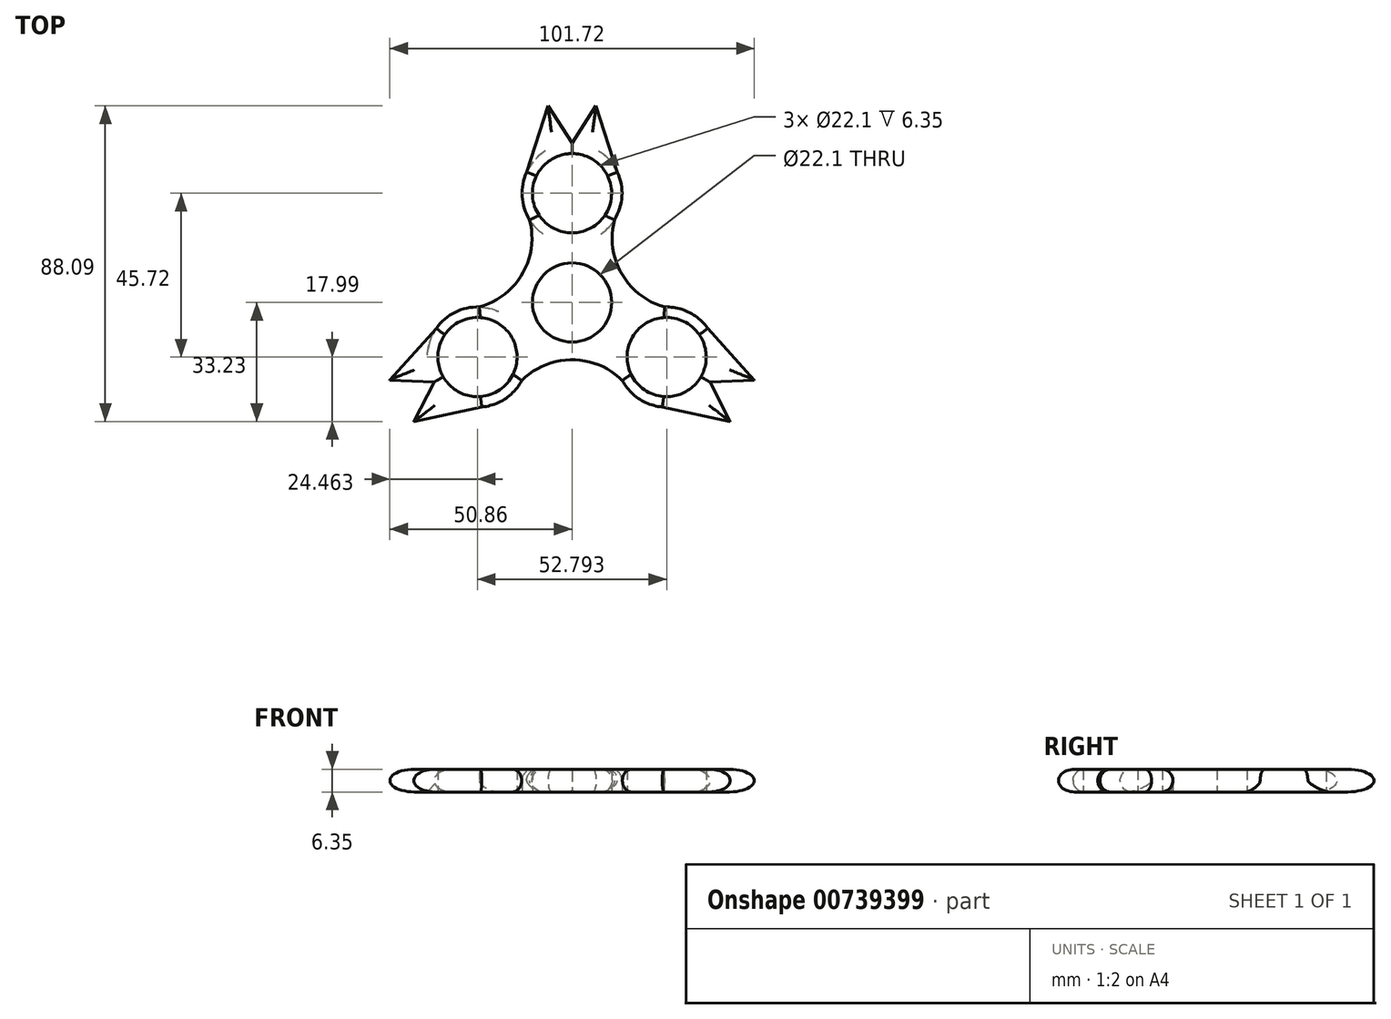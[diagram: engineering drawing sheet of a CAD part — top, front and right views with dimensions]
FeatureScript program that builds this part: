
annotation { "Feature Type Name" : "Feature", "Feature Type Description" : "" }
export const myFeature = defineFeature(function(context is Context, id is Id, definition is map)
    precondition{}
    {
        {
            var Q0;
            Q0=qCreatedBy(makeId("Top.planeOp"),FACE);
            var sketch = newSketch(context, id + "F0", { "sketchPlane" : qUnion([Q0])});
            skCircle(sketch, "E0", {"center": v(0, 0) * mm, "radius": 11.05 * mm});
            skLineSegment(sketch, "E1", {"start": v(0, 0) * mm, "end": v(0, 30.48) * mm});
            skCircle(sketch, "E2", {"center": v(0, 30.48) * mm, "radius": 11.05 * mm});
            skArc(sketch, "E3", {"start": v(-12.66, 36.38) * mm, "mid": v(-13.94, 29.62) * mm, "end": v(-11.84, 23.06) * mm});
            skCircle(sketch, "E4.1.0", {"center": v(-26.4, -15.24) * mm, "radius": 11.05 * mm});
            skArc(sketch, "E4.1.1", {"start": v(-25.17, -29.16) * mm, "mid": v(-18.68, -26.88) * mm, "end": v(-14.05, -21.79) * mm});
            skCircle(sketch, "E4.2.0", {"center": v(26.4, -15.24) * mm, "radius": 11.05 * mm});
            skArc(sketch, "E4.2.1", {"start": v(14.05, -21.79) * mm, "mid": v(18.68, -26.88) * mm, "end": v(25.17, -29.16) * mm});
            skLineSegment(sketch, "E5", {"start": v(0, 0) * mm, "end": v(-44.44, 25.66) * mm});
            skArc(sketch, "E6", {"start": v(-30.75, -1.97) * mm, "mid": v(-13.84, 8) * mm, "end": v(-13.67, 27.61) * mm});
            skArc(sketch, "E7.1.0", {"start": v(17.08, -25.65) * mm, "mid": v(0, -15.98) * mm, "end": v(-17.08, -25.65) * mm});
            skArc(sketch, "E7.2.0", {"start": v(13.67, 27.61) * mm, "mid": v(13.84, 8) * mm, "end": v(30.75, -1.97) * mm});
            skLineSegment(sketch, "E8", {"start": v(-12.66, 36.38) * mm, "end": v(-6.7, 54.86) * mm});
            skLineSegment(sketch, "E9", {"start": v(-6.7, 54.86) * mm, "end": v(0, 44.45) * mm});
            skLineSegment(sketch, "E10.MirrorCS", {"start": v(12.66, 36.38) * mm, "end": v(6.7, 54.86) * mm});
            skLineSegment(sketch, "E11.MirrorCS", {"start": v(6.7, 54.86) * mm, "end": v(0, 44.45) * mm});
            skLineSegment(sketch, "E12.1.0", {"start": v(-25.17, -29.16) * mm, "end": v(-44.17, -33.23) * mm});
            skLineSegment(sketch, "E12.1.1", {"start": v(-44.17, -33.23) * mm, "end": v(-38.5, -22.22) * mm});
            skLineSegment(sketch, "E12.1.2", {"start": v(-50.86, -21.64) * mm, "end": v(-38.5, -22.22) * mm});
            skLineSegment(sketch, "E12.1.3", {"start": v(-37.84, -7.22) * mm, "end": v(-50.86, -21.64) * mm});
            skLineSegment(sketch, "E12.2.0", {"start": v(37.84, -7.22) * mm, "end": v(50.86, -21.64) * mm});
            skLineSegment(sketch, "E12.2.1", {"start": v(50.86, -21.64) * mm, "end": v(38.5, -22.23) * mm});
            skLineSegment(sketch, "E12.2.2", {"start": v(44.17, -33.23) * mm, "end": v(38.5, -22.23) * mm});
            skLineSegment(sketch, "E12.2.3", {"start": v(25.17, -29.16) * mm, "end": v(44.17, -33.23) * mm});
            skArc(sketch, "E13.trimOffspring", {"start": v(11.84, 23.06) * mm, "mid": v(13.94, 29.62) * mm, "end": v(12.66, 36.38) * mm});
            skArc(sketch, "E14.trimOffspring", {"start": v(-25.9, -1.28) * mm, "mid": v(-32.62, -2.73) * mm, "end": v(-37.84, -7.22) * mm});
            skArc(sketch, "E15.trimOffspring", {"start": v(37.84, -7.22) * mm, "mid": v(32.62, -2.73) * mm, "end": v(25.9, -1.28) * mm});
            skSolve(sketch);
        }
        {
            var Q0;
            Q0 = qSketchRegion(id + "F0", true);
            extrude(context, id + "F1", {"entities" : qUnion([Q0]), "depth" : 6.35 * mm, "offsetDistance" : 25.4 * mm});
        }
        {
            var Q0;
            Q0=makeQuery(id+"F1.opExtrude","CAP_EDGE",EDGE,{"disambiguationData":[OSD([sQuery(id+"F0.wireOp",EDGE,"E3")])],"isStart":false});
            var Q1;
            Q1=makeQuery(id+"F1.opExtrude","CAP_EDGE",EDGE,{"disambiguationData":[OSD([sQuery(id+"F0.wireOp",EDGE,"E6")])],"isStart":false});
            var Q2;
            Q2=makeQuery(id+"F1.opExtrude","CAP_EDGE",EDGE,{"disambiguationData":[OSD([sQuery(id+"F0.wireOp",EDGE,"E14.trimOffspring")])],"isStart":false});
            var Q3;
            Q3=makeQuery(id+"F1.opExtrude","CAP_EDGE",EDGE,{"disambiguationData":[OSD([sQuery(id+"F0.wireOp",EDGE,"E6")])],"isStart":true});
            var Q4;
            Q4=makeQuery(id+"F1.opExtrude","CAP_EDGE",EDGE,{"disambiguationData":[OSD([sQuery(id+"F0.wireOp",EDGE,"E7.2.0")])],"isStart":false});
            var Q5;
            Q5=makeQuery(id+"F1.opExtrude","CAP_EDGE",EDGE,{"disambiguationData":[OSD([sQuery(id+"F0.wireOp",EDGE,"E13.trimOffspring")])],"isStart":false});
            var Q6;
            Q6=makeQuery(id+"F1.opExtrude","CAP_EDGE",EDGE,{"disambiguationData":[OSD([sQuery(id+"F0.wireOp",EDGE,"E7.2.0")])],"isStart":true});
            var Q7;
            Q7=makeQuery(id+"F1.opExtrude","CAP_EDGE",EDGE,{"disambiguationData":[OSD([sQuery(id+"F0.wireOp",EDGE,"E15.trimOffspring")])],"isStart":true});
            var Q8;
            Q8=makeQuery(id+"F1.opExtrude","CAP_EDGE",EDGE,{"disambiguationData":[OSD([sQuery(id+"F0.wireOp",EDGE,"E4.2.1")])],"isStart":false});
            var Q9;
            Q9=makeQuery(id+"F1.opExtrude","CAP_EDGE",EDGE,{"disambiguationData":[OSD([sQuery(id+"F0.wireOp",EDGE,"E7.1.0")])],"isStart":false});
            var Q10;
            Q10=makeQuery(id+"F1.opExtrude","CAP_EDGE",EDGE,{"disambiguationData":[OSD([sQuery(id+"F0.wireOp",EDGE,"E4.1.1")])],"isStart":false});
            var Q11;
            Q11=makeQuery(id+"F1.opExtrude","CAP_EDGE",EDGE,{"disambiguationData":[OSD([sQuery(id+"F0.wireOp",EDGE,"E7.1.0")])],"isStart":true});
            var Q12;
            Q12=makeQuery(id+"F1.opExtrude","CAP_EDGE",EDGE,{"disambiguationData":[OSD([sQuery(id+"F0.wireOp",EDGE,"E4.1.1")])],"isStart":true});
            var Q13;
            Q13=makeQuery(id+"F1.opExtrude","CAP_EDGE",EDGE,{"disambiguationData":[OSD([sQuery(id+"F0.wireOp",EDGE,"E4.2.1")])],"isStart":true});
            var Q14;
            Q14=makeQuery(id+"F1.opExtrude","CAP_EDGE",EDGE,{"disambiguationData":[OSD([sQuery(id+"F0.wireOp",EDGE,"E12.1.3")])],"isStart":true});
            var Q15;
            Q15=makeQuery(id+"F1.opExtrude","CAP_EDGE",EDGE,{"disambiguationData":[OSD([sQuery(id+"F0.wireOp",EDGE,"E12.1.2")])],"isStart":true});
            var Q16;
            Q16=makeQuery(id+"F1.opExtrude","CAP_EDGE",EDGE,{"disambiguationData":[OSD([sQuery(id+"F0.wireOp",EDGE,"E12.1.0")])],"isStart":true});
            var Q17;
            Q17=makeQuery(id+"F1.opExtrude","CAP_EDGE",EDGE,{"disambiguationData":[OSD([sQuery(id+"F0.wireOp",EDGE,"E12.1.1")])],"isStart":true});
            var Q18;
            Q18=makeQuery(id+"F1.opExtrude","CAP_EDGE",EDGE,{"disambiguationData":[OSD([sQuery(id+"F0.wireOp",EDGE,"E12.2.3")])],"isStart":true});
            var Q19;
            Q19=makeQuery(id+"F1.opExtrude","CAP_EDGE",EDGE,{"disambiguationData":[OSD([sQuery(id+"F0.wireOp",EDGE,"E12.2.2")])],"isStart":true});
            var Q20;
            Q20=makeQuery(id+"F1.opExtrude","CAP_EDGE",EDGE,{"disambiguationData":[OSD([sQuery(id+"F0.wireOp",EDGE,"E12.2.1")])],"isStart":true});
            var Q21;
            Q21=makeQuery(id+"F1.opExtrude","CAP_EDGE",EDGE,{"disambiguationData":[OSD([sQuery(id+"F0.wireOp",EDGE,"E12.2.0")])],"isStart":true});
            var Q22;
            Q22=makeQuery(id+"F1.opExtrude","CAP_EDGE",EDGE,{"disambiguationData":[OSD([sQuery(id+"F0.wireOp",EDGE,"E10.MirrorCS")])],"isStart":true});
            var Q23;
            Q23=makeQuery(id+"F1.opExtrude","CAP_EDGE",EDGE,{"disambiguationData":[OSD([sQuery(id+"F0.wireOp",EDGE,"E8")])],"isStart":true});
            var Q24;
            Q24=makeQuery(id+"F1.opExtrude","CAP_EDGE",EDGE,{"disambiguationData":[OSD([sQuery(id+"F0.wireOp",EDGE,"E11.MirrorCS")])],"isStart":true});
            var Q25;
            Q25=makeQuery(id+"F1.opExtrude","CAP_EDGE",EDGE,{"disambiguationData":[OSD([sQuery(id+"F0.wireOp",EDGE,"E9")])],"isStart":true});
            var Q26;
            Q26=makeQuery(id+"F1.opExtrude","CAP_EDGE",EDGE,{"disambiguationData":[OSD([sQuery(id+"F0.wireOp",EDGE,"E12.2.3")])],"isStart":false});
            var Q27;
            Q27=makeQuery(id+"F1.opExtrude","CAP_EDGE",EDGE,{"disambiguationData":[OSD([sQuery(id+"F0.wireOp",EDGE,"E12.1.0")])],"isStart":false});
            var Q28;
            Q28=makeQuery(id+"F1.opExtrude","CAP_EDGE",EDGE,{"disambiguationData":[OSD([sQuery(id+"F0.wireOp",EDGE,"E12.1.3")])],"isStart":false});
            var Q29;
            Q29=makeQuery(id+"F1.opExtrude","CAP_EDGE",EDGE,{"disambiguationData":[OSD([sQuery(id+"F0.wireOp",EDGE,"E11.MirrorCS")])],"isStart":false});
            var Q30;
            Q30=makeQuery(id+"F1.opExtrude","CAP_EDGE",EDGE,{"disambiguationData":[OSD([sQuery(id+"F0.wireOp",EDGE,"E8")])],"isStart":false});
            var Q31;
            Q31=makeQuery(id+"F1.opExtrude","CAP_EDGE",EDGE,{"disambiguationData":[OSD([sQuery(id+"F0.wireOp",EDGE,"E9")])],"isStart":false});
            var Q32;
            Q32=makeQuery(id+"F1.opExtrude","CAP_EDGE",EDGE,{"disambiguationData":[OSD([sQuery(id+"F0.wireOp",EDGE,"E10.MirrorCS")])],"isStart":false});
            var Q33;
            Q33=makeQuery(id+"F1.opExtrude","CAP_EDGE",EDGE,{"disambiguationData":[OSD([sQuery(id+"F0.wireOp",EDGE,"E12.2.0")])],"isStart":false});
            var Q34;
            Q34=makeQuery(id+"F1.opExtrude","CAP_EDGE",EDGE,{"disambiguationData":[OSD([sQuery(id+"F0.wireOp",EDGE,"E15.trimOffspring")])],"isStart":false});
            var Q35;
            Q35=makeQuery(id+"F1.opExtrude","CAP_EDGE",EDGE,{"disambiguationData":[OSD([sQuery(id+"F0.wireOp",EDGE,"E12.2.1")])],"isStart":false});
            var Q36;
            Q36=makeQuery(id+"F1.opExtrude","CAP_EDGE",EDGE,{"disambiguationData":[OSD([sQuery(id+"F0.wireOp",EDGE,"E12.2.2")])],"isStart":false});
            var Q37;
            Q37=makeQuery(id+"F1.opExtrude","CAP_EDGE",EDGE,{"disambiguationData":[OSD([sQuery(id+"F0.wireOp",EDGE,"E12.1.2")])],"isStart":false});
            var Q38;
            Q38=makeQuery(id+"F1.opExtrude","CAP_EDGE",EDGE,{"disambiguationData":[OSD([sQuery(id+"F0.wireOp",EDGE,"E12.1.1")])],"isStart":false});
            fillet(context, id + "F2", {"entities" : qUnion([Q0, Q1, Q2, Q3, Q4, Q5, Q6, Q7, Q8, Q9, Q10, Q11, Q12, Q13, Q14, Q15, Q16, Q17, Q18, Q19, Q20, Q21, Q22, Q23, Q24, Q25, Q26, Q27, Q28, Q29, Q30, Q31, Q32, Q33, Q34, Q35, Q36, Q37, Q38]), "radius" : 3.17 * mm, "tangentPropagation" : true, "allowEdgeOverflow" : false});
        }
    });
